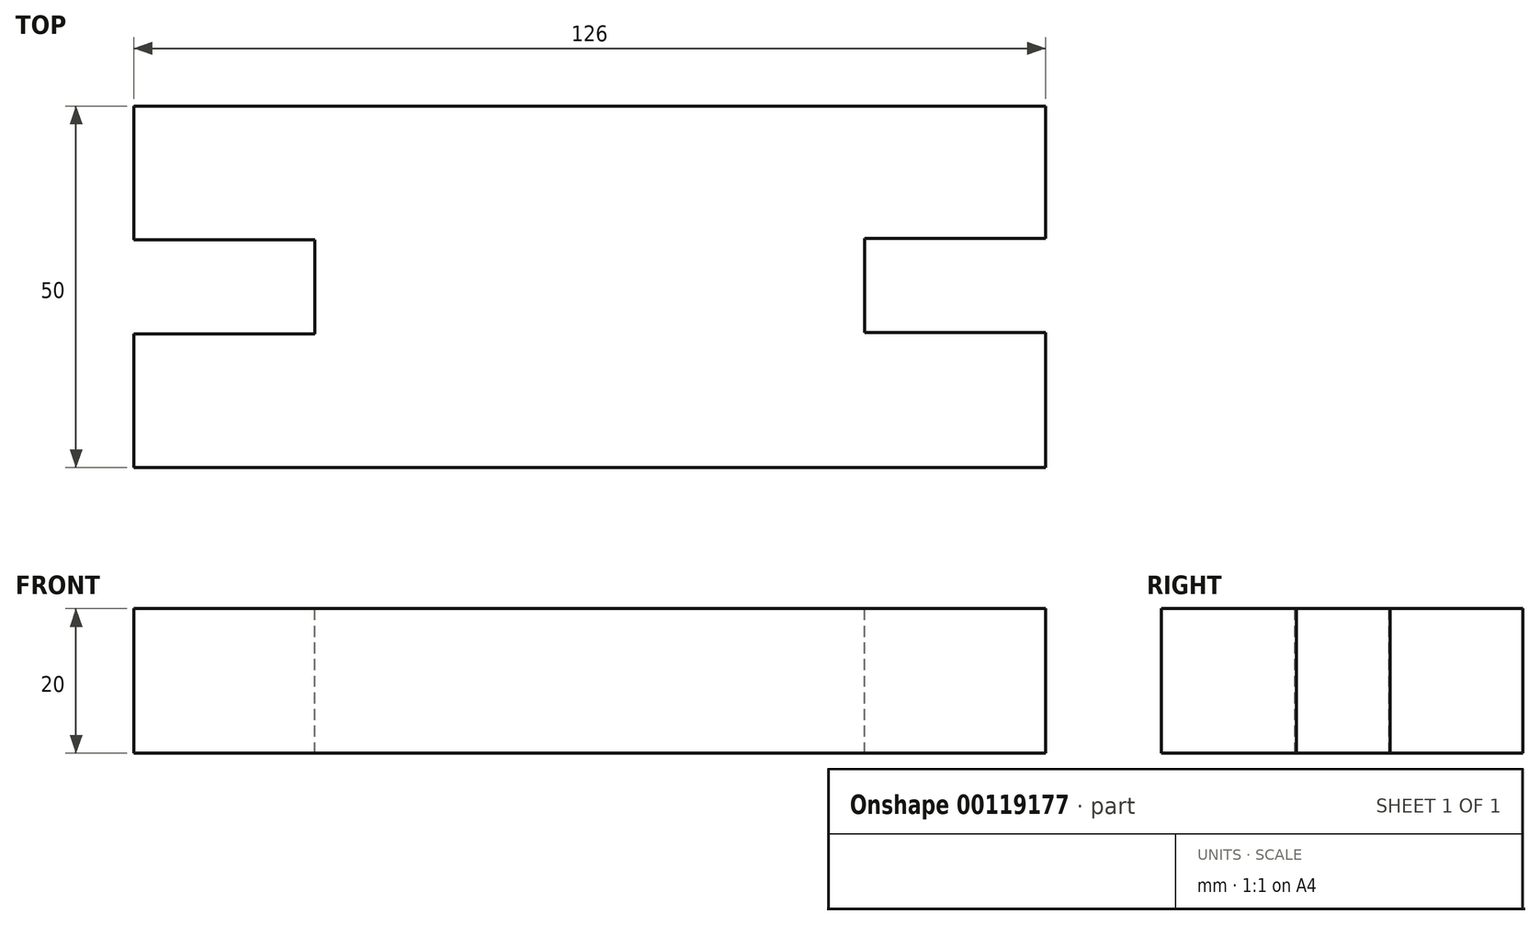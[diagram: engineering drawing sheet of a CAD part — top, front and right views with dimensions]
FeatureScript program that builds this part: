
annotation { "Feature Type Name" : "Feature", "Feature Type Description" : "" }
export const myFeature = defineFeature(function(context is Context, id is Id, definition is map)
    precondition{}
    {
        {
            var Q0;
            Q0=qCreatedBy(makeId("Front.planeOp"),FACE);
            var sketch = newSketch(context, id + "F0", { "sketchPlane" : qUnion([Q0])});
            skLineSegment(sketch, "E0.bottom", {"start": v(-45.23, 29.73) * mm, "end": v(80.77, 29.73) * mm});
            skLineSegment(sketch, "E0.top", {"start": v(-45.23, 9.73) * mm, "end": v(80.77, 9.73) * mm});
            skLineSegment(sketch, "E0.left", {"start": v(-45.23, 29.73) * mm, "end": v(-45.23, 9.73) * mm});
            skLineSegment(sketch, "E0.right", {"start": v(80.77, 29.73) * mm, "end": v(80.77, 9.73) * mm});
            skSolve(sketch);
        }
        {
            var Q0;
            Q0=makeQuery(id+"F0.imprint","IMPRINT",FACE,{"disambiguationData":[TD([[makeQuery(id+"F0.imprint","IMPRINT",EDGE,{"derivedFrom":sQuery(id+"F0.wireOp",EDGE,"E0.bottom")}),-1.0]])]});
            extrude(context, id + "F1", {"entities" : qUnion([Q0]), "endBound" : BoundingType.SYMMETRIC, "depth" : 50 * mm});
        }
        {
            var Q0;
            Q0=makeQuery(id+"F1.opExtrude","SWEPT_FACE",FACE,{"disambiguationData":[OSD([sQuery(id+"F0.wireOp",EDGE,"E0.bottom")])]});
            var sketch = newSketch(context, id + "F2", { "sketchPlane" : qUnion([Q0])});
            skLineSegment(sketch, "E1.bottom", {"start": v(-45.23, 6.5) * mm, "end": v(-20.23, 6.5) * mm});
            skLineSegment(sketch, "E1.top", {"start": v(-45.23, -6.5) * mm, "end": v(-20.23, -6.5) * mm});
            skLineSegment(sketch, "E1.left", {"start": v(-45.23, 6.5) * mm, "end": v(-45.23, -6.5) * mm});
            skLineSegment(sketch, "E1.right", {"start": v(-20.23, 6.5) * mm, "end": v(-20.23, -6.5) * mm});
            skLineSegment(sketch, "E2.bottom", {"start": v(80.77, -6.33) * mm, "end": v(55.77, -6.33) * mm});
            skLineSegment(sketch, "E2.top", {"start": v(80.77, 6.67) * mm, "end": v(55.77, 6.67) * mm});
            skLineSegment(sketch, "E2.left", {"start": v(80.77, -6.33) * mm, "end": v(80.77, 6.67) * mm});
            skLineSegment(sketch, "E2.right", {"start": v(55.77, -6.33) * mm, "end": v(55.77, 6.67) * mm});
            skSolve(sketch);
        }
        {
            var Q0;
            Q0 = qSketchRegion(id + "F2", true);
            extrude(context, id + "F3", {"entities" : qUnion([Q0]), "operationType" : NewBodyOperationType.REMOVE, "endBound" : BoundingType.THROUGH_ALL, "oppositeDirection" : true, "depth" : 25 * mm});
        }
    });
